FREECAD ASSEMBLY — COMPONENT RECIPES ("asm_roof")

This assembly document has 11 components, labeled P0..P10 below (a component is one placed body or linked part). 3 of them carry a construction recipe — the FreeCAD feature program that regenerates the part from scratch, quoted from this document or its linked companion documents; the rest are supplied as boundary geometry only. No exploded tour is included for this assembly.
COMPONENT P0 — geometry summary ("Hexagonal Nut M4_CBALN005"; no construction recipe available for this part):
  bounding box: 8.1 x 7.0 x 3.2 mm
  tessellated surface: 2,828 triangles
  volume: 100 mm^3 (55% of its bounding box)
  symmetry: 6-fold rotationally symmetric about the z axis
COMPONENT P1 — geometry summary ("Hexagonal Nut M4_CBALN006"; no construction recipe available for this part):
  bounding box: 8.1 x 7.0 x 3.2 mm
  tessellated surface: 2,828 triangles
  volume: 100 mm^3 (55% of its bounding box)
  symmetry: 6-fold rotationally symmetric about the z axis
COMPONENT P2 — geometry summary ("Hexagonal Nut M4_CBALN007"; no construction recipe available for this part):
  bounding box: 8.1 x 7.0 x 3.2 mm
  tessellated surface: 2,828 triangles
  volume: 100 mm^3 (55% of its bounding box)
  symmetry: 6-fold rotationally symmetric about the z axis
COMPONENT P3 — geometry summary ("Hexagonal Nut M4_CBALN4"; no construction recipe available for this part):
  bounding box: 8.1 x 7.0 x 3.2 mm
  tessellated surface: 2,828 triangles
  volume: 100 mm^3 (55% of its bounding box)
  symmetry: 6-fold rotationally symmetric about the z axis
COMPONENT P4 — geometry summary ("Hexagonal Nut M5_CBALN006"; no construction recipe available for this part):
  bounding box: 9.2 x 8.0 x 4.0 mm
  tessellated surface: 3,728 triangles
  volume: 149 mm^3 (51% of its bounding box)
COMPONENT P5 — geometry summary ("Hexagonal Nut M5_CBALN007"; no construction recipe available for this part):
  bounding box: 9.2 x 8.0 x 4.0 mm
  tessellated surface: 3,728 triangles
  volume: 149 mm^3 (51% of its bounding box)
COMPONENT P6 — geometry summary ("Hexagonal Nut M5_CBALN008"; no construction recipe available for this part):
  bounding box: 9.2 x 8.0 x 4.0 mm
  tessellated surface: 3,728 triangles
  volume: 149 mm^3 (51% of its bounding box)
COMPONENT P7 — geometry summary ("Hexagonal Nut M5_CBALN5"; no construction recipe available for this part):
  bounding box: 9.2 x 8.0 x 4.0 mm
  tessellated surface: 3,728 triangles
  volume: 149 mm^3 (51% of its bounding box)
COMPONENT P8 — recipe-attached ("linear_slide_12", a linked part whose construction recipe lives in a companion FreeCAD document of the same project; that document's serialized recipe follows).
Construction recipe (the companion document, serialized — sketch geometry with constraints, then the solid features built on it; lengths are millimeters unless a unit is written):

FCSTD DOCUMENT  (FreeCAD 1.0R39109 (Git))
Label: linear_slide
License: All rights reserved
LicenseURL: https://en.wikipedia.org/wiki/All_rights_reserved
objects: Sketcher::SketchObject×1, PartDesign::Pad×1, PartDesign::Body×1
note: 6 computed .brp shape members not serialized (recipe doc carries the construction recipe); baked Part::Feature solids carry a one-line shape summary decoded from their .brp

FEATURE [Sketcher::SketchObject] Sketch
  ArcFitTolerance = 1e-06
  AttachmentSupport = -> [XY_Plane]
  FullyConstrained = true
  MakeInternals = false
  MapMode = 5
  sketch-geometry (1):
    g0: Circle CenterX=0 CenterY=0 CenterZ=0 NormalX=0 NormalY=0 NormalZ=1 AngleXU=0 Radius=6
  constraints (2):
    c: Coincident(g0,g-1)
    c: Diameter(g0) = 12
FEATURE [PartDesign::Pad] Pad
  Direction = (0,0,1)
  Length = 100
  Length2 = 10
  Profile = -> Sketch
  ReferenceAxis = -> Sketch [N_Axis]
  Refine = true
  Suppressed = false
  Type = 0
FEATURE [PartDesign::Body] Body  label="linear_slide_12"
  AllowCompound = false
  Group = -> [Sketch,Pad]
  Origin = -> Origin
  Tip = -> Pad
COMPONENT P9 — same part as P8; its construction recipe is shown at P8.
COMPONENT P10 — recipe-attached ("plate_roof", a linked part whose construction recipe lives in a companion FreeCAD document of the same project; that document's serialized recipe follows).
Construction recipe (the companion document, serialized — sketch geometry with constraints, then the solid features built on it; lengths are millimeters unless a unit is written):

FCSTD DOCUMENT  (FreeCAD 1.0R38641 +468 (Git))
Label: plate_roof
License: All rights reserved
LicenseURL: https://en.wikipedia.org/wiki/All_rights_reserved
objects: TechDraw::DrawViewDimension×10, TechDraw::DrawProjGroupItem×2, Sketcher::SketchObject×1, PartDesign::Pad×1, PartDesign::Body×1, TechDraw::DrawSVGTemplate×1, TechDraw::DrawProjGroup×1, TechDraw::DrawPage×1
note: 22 computed .brp shape members not serialized (recipe doc carries the construction recipe); baked Part::Feature solids carry a one-line shape summary decoded from their .brp

FEATURE [Sketcher::SketchObject] Sketch
  ArcFitTolerance = 1e-06
  AttachmentSupport = -> [XY_Plane]
  FullyConstrained = false
  MakeInternals = false
  MapMode = 5
  sketch-geometry (16):
    g0: LineSegment StartX=-100 StartY=200 StartZ=0 EndX=-100 EndY=-200 EndZ=0
    g1: LineSegment StartX=-100 StartY=-200 StartZ=0 EndX=100 EndY=-200 EndZ=0
    g2: LineSegment StartX=100 StartY=-200 StartZ=0 EndX=100 EndY=200 EndZ=0
    g3: LineSegment StartX=100 StartY=200 StartZ=0 EndX=-100 EndY=200 EndZ=0
    g4: Circle CenterX=-44 CenterY=50.2 CenterZ=0 NormalX=0 NormalY=0 NormalZ=1 AngleXU=0 Radius=2.45
    g5: Circle CenterX=-44 CenterY=-157.8 CenterZ=0 NormalX=0 NormalY=0 NormalZ=1 AngleXU=0 Radius=2.45
    g6: Circle CenterX=44 CenterY=50.2 CenterZ=0 NormalX=0 NormalY=0 NormalZ=1 AngleXU=0 Radius=2.45
    g7: Circle CenterX=44 CenterY=-157.8 CenterZ=0 NormalX=0 NormalY=0 NormalZ=1 AngleXU=0 Radius=2.45
    g8: Circle [constr] CenterX=0 CenterY=0 CenterZ=0 NormalX=0 NormalY=0 NormalZ=1 AngleXU=0 Radius=9.44112
    g9: Circle CenterX=-38 CenterY=-35.8 CenterZ=0 NormalX=0 NormalY=0 NormalZ=1 AngleXU=0 Radius=1.95
    g10: Circle CenterX=-38 CenterY=-71.8 CenterZ=0 NormalX=0 NormalY=0 NormalZ=1 AngleXU=0 Radius=1.95
    g11: Circle CenterX=-38 CenterY=-53.8 CenterZ=0 NormalX=0 NormalY=0 NormalZ=1 AngleXU=0 Radius=6.5
    g12: Circle CenterX=38 CenterY=-35.8 CenterZ=0 NormalX=0 NormalY=0 NormalZ=1 AngleXU=0 Radius=1.95
    g13: Circle CenterX=38 CenterY=-53.8 CenterZ=0 NormalX=0 NormalY=0 NormalZ=1 AngleXU=0 Radius=6.5
    g14: Circle CenterX=38 CenterY=-71.8 CenterZ=0 NormalX=0 NormalY=0 NormalZ=1 AngleXU=0 Radius=1.95
    g15: LineSegment [constr] StartX=0 StartY=0 StartZ=0 EndX=0 EndY=174.663 EndZ=0
  constraints (44):
    c: Coincident(g0,g1)
    c: Coincident(g1,g2)
    c: Coincident(g2,g3)
    c: Coincident(g3,g0)
    c: Vertical(g0)
    c: Vertical(g2)
    c: Horizontal(g1)
    c: Horizontal(g3)
    c: DistanceY(g0,g0) = 400
    c: DistanceX(g3,g3) = 200
    c: Vertical(g4,g5)
    c: Diameter(g4) = 4.9
    c: Equal(g4,g5)
    c: DistanceY(g5,g4) = 208
    c: Horizontal(g6,g4)
    c: Horizontal(g7,g5)
    c: Equal(g6,g4)
    c: Equal(g4,g7)
    c: DistanceX(g4,g6) = 88
    c: Vertical(g7,g6)
    c: DistanceY(g8,g4) = 50.2
    c: DistanceX(g4,g8) = 44
    c: Distance(g8,g3) = 200
    c: Distance(g8,g0) = 100
    c: Vertical(g9,g11)
    c: Vertical(g11,g10)
    c: Vertical(g12,g13)
    c: Vertical(g13,g14)
    c: DistanceY(g11,g9) = 18
    c: DistanceY(g10,g11) = 18
    c: Diameter(g9) = 3.9
    c: Equal(g9,g10)
    c: Equal(g10,g12)
    c: Equal(g12,g14)
    c: Horizontal(g9,g12)
    c: Horizontal(g10,g14)
    c: Equal(g11,g13)
    c: Diameter(g11) = 13
    c: DistanceX(g11,g8) = 38
    c: Horizontal(g11,g13)
    c: DistanceY(g11,g4) = 104
    c: Coincident(g15,g8)
    c: Symmetric(g11,g13,g15)
    c: Coincident(g8,g-1)
FEATURE [PartDesign::Pad] Pad
  Direction = (0,0,1)
  Length = 3
  Length2 = 10
  Profile = -> Sketch
  ReferenceAxis = -> Sketch [N_Axis]
  Refine = true
  Suppressed = false
  Type = 0
FEATURE [PartDesign::Body] Body  label="plate_roof"
  AllowCompound = false
  Group = -> [Sketch,Pad]
  Origin = -> Origin
  Tip = -> Pad
FEATURE [TechDraw::DrawSVGTemplate] Template
  EditableTexts = approval_person=B. Hecate; creator=Djordje Vujic; date_of_issue=20.1.25.; document_type=Assembly Drawing; general_tolerances=ISO 2768-m; identification_number=DN; language_code=EN; part_material=Stainless steel Mat.No. 1.4301; revision_index=AAA; sheet_number=1 / 3; sheet_scale=1 : 2; title=plate_roof
  Height = 297
  Orientation = 0
  Template = /snap/freecad/1248/usr/share/Mod/TechDraw/Templates/A4_Portrait_ISO5457_minimal.svg
  Width = 210
FEATURE [TechDraw::DrawProjGroupItem] ProjItem  label="Front"
  CoarseView = false
  Direction = (0,0,1)
  Focus = 100
  HardHidden = false
  IsoCount = 0
  IsoHidden = false
  IsoVisible = false
  LockPosition = true
  Perspective = false
  Rotation = 0
  RotationVector = (1,0,0)
  Scale = 0.5
  ScaleType = 0
  ScrubCount = 1
  SeamHidden = false
  SeamVisible = false
  SmoothHidden = false
  SmoothVisible = true
  Source = -> [Body]
  Type = 0
  X = 0
  XDirection = (1,0,0)
  Y = 0
FEATURE [TechDraw::DrawProjGroupItem] ProjItem001  label="Bottom"
  CoarseView = false
  Direction = (0,-1,0)
  Focus = 100
  HardHidden = false
  IsoCount = 0
  IsoHidden = false
  IsoVisible = false
  LockPosition = false
  Perspective = false
  Rotation = 0
  RotationVector = (1,0,0)
  Scale = 0.5
  ScaleType = 0
  ScrubCount = 1
  SeamHidden = false
  SeamVisible = false
  SmoothHidden = false
  SmoothVisible = true
  Source = -> [Body]
  Type = 5
  X = 0
  XDirection = (1,0,0)
  Y = 115.75
FEATURE [TechDraw::DrawProjGroup] ProjGroup
  Anchor = -> ProjItem
  AutoDistribute = true
  LockPosition = false
  ProjectionType = 0
  Rotation = 0
  Scale = 0.5
  ScaleType = 2
  Source = -> [Body]
  Views = -> [ProjItem,ProjItem001]
  X = 105
  Y = 162.983
  spacingX = 15
  spacingY = 15
FEATURE [TechDraw::DrawViewDimension] Dimension
  AngleOverride = false
  Arbitrary = false
  ArbitraryTolerances = false
  BoxCorners = (2) [(-50,-0.75,0),(50,0.75,0)]
  EqualTolerance = true
  ExtensionAngle = 0
  FormatSpec = %.2w
  FormatSpecOverTolerance = %+.2w
  FormatSpecUnderTolerance = %+.2w
  Inverted = false
  LineAngle = 0
  LockPosition = false
  MeasureType = 1
  OverTolerance = 0
  References2D = -> [ProjItem001]
  Rotation = 0
  ScaleType = 0
  TheoreticalExact = false
  Type = 2
  UnderTolerance = 0
  X = -62.2509
  Y = -6.95305
FEATURE [TechDraw::DrawViewDimension] Dimension001
  AngleOverride = false
  Arbitrary = false
  ArbitraryTolerances = false
  BoxCorners = (2) [(-50,-0.75,0),(50,0.75,0)]
  EqualTolerance = true
  ExtensionAngle = 0
  FormatSpec = %.2w
  FormatSpecOverTolerance = %+.2w
  FormatSpecUnderTolerance = %+.2w
  Inverted = false
  LineAngle = 0
  LockPosition = false
  MeasureType = 1
  OverTolerance = 0
  References2D = -> [ProjItem001]
  Rotation = 0
  ScaleType = 0
  TheoreticalExact = false
  Type = 1
  UnderTolerance = 0
  X = 0
  Y = -5.41651
FEATURE [TechDraw::DrawViewDimension] Dimension002
  AngleOverride = false
  Arbitrary = false
  ArbitraryTolerances = false
  BoxCorners = (2) [(-50,-100,0),(50,100,0)]
  EqualTolerance = true
  ExtensionAngle = 0
  FormatSpec = %.2w
  FormatSpecOverTolerance = %+.2w
  FormatSpecUnderTolerance = %+.2w
  Inverted = false
  LineAngle = 0
  LockPosition = false
  MeasureType = 1
  OverTolerance = 0
  References2D = -> [ProjItem]
  Rotation = 0
  ScaleType = 0
  TheoreticalExact = false
  Type = 2
  UnderTolerance = 0
  X = -64.6458
  Y = 3.29053
FEATURE [TechDraw::DrawViewDimension] Dimension003
  AngleOverride = false
  Arbitrary = false
  ArbitraryTolerances = false
  BoxCorners = (2) [(-50,-100,0),(50,100,0)]
  EqualTolerance = true
  ExtensionAngle = 0
  FormatSpec = %.2w
  FormatSpecOverTolerance = %+.2w
  FormatSpecUnderTolerance = %+.2w
  Inverted = false
  LineAngle = 0
  LockPosition = false
  MeasureType = 1
  OverTolerance = 0
  References2D = -> [ProjItem]
  Rotation = 0
  ScaleType = 0
  TheoreticalExact = false
  Type = 0
  UnderTolerance = 0
  X = 29.0917
  Y = -31.4
FEATURE [TechDraw::DrawViewDimension] Dimension004
  AngleOverride = false
  Arbitrary = false
  ArbitraryTolerances = false
  BoxCorners = (2) [(-50,-100,0),(50,100,0)]
  EqualTolerance = true
  ExtensionAngle = 0
  FormatSpec = %.2w
  FormatSpecOverTolerance = %+.2w
  FormatSpecUnderTolerance = %+.2w
  Inverted = false
  LineAngle = 0
  LockPosition = false
  MeasureType = 1
  OverTolerance = 0
  References2D = -> [ProjItem]
  Rotation = 0
  ScaleType = 0
  TheoreticalExact = false
  Type = 0
  UnderTolerance = 0
  X = 0
  Y = -5.52183
FEATURE [TechDraw::DrawViewDimension] Dimension005
  AngleOverride = false
  Arbitrary = false
  ArbitraryTolerances = false
  BoxCorners = (2) [(-50,-100,0),(50,100,0)]
  EqualTolerance = true
  ExtensionAngle = 0
  FormatSpec = %.2w
  FormatSpecOverTolerance = %+.2w
  FormatSpecUnderTolerance = %+.2w
  Inverted = false
  LineAngle = 0
  LockPosition = false
  MeasureType = 1
  OverTolerance = 0
  References2D = -> [ProjItem]
  Rotation = 0
  ScaleType = 0
  TheoreticalExact = false
  Type = 0
  UnderTolerance = 0
  X = -34.5
  Y = -5.52183
FEATURE [TechDraw::DrawViewDimension] Dimension006
  AngleOverride = false
  Arbitrary = false
  ArbitraryTolerances = false
  BoxCorners = (2) [(-50,-100,0),(50,100,0)]
  EqualTolerance = true
  ExtensionAngle = 0
  FormatSpec = %.2w
  FormatSpecOverTolerance = %+.2w
  FormatSpecUnderTolerance = %+.2w
  Inverted = false
  LineAngle = 0
  LockPosition = false
  MeasureType = 1
  OverTolerance = 0
  References2D = -> [ProjItem]
  Rotation = 0
  ScaleType = 0
  TheoreticalExact = false
  Type = 0
  UnderTolerance = 0
  X = -33.0527
  Y = -22.4
FEATURE [TechDraw::DrawViewDimension] Dimension007
  AngleOverride = false
  Arbitrary = false
  ArbitraryTolerances = false
  BoxCorners = (2) [(-50,-100,0),(50,100,0)]
  EqualTolerance = false
  ExtensionAngle = 0
  FormatSpec = ⌀%.2w
  FormatSpecOverTolerance = %+.2w
  FormatSpecUnderTolerance = -%.2w
  Inverted = false
  LineAngle = 0
  LockPosition = false
  MeasureType = 1
  OverTolerance = 1
  References2D = -> [ProjItem]
  Rotation = 0
  ScaleType = 0
  TheoreticalExact = false
  Type = 5
  UnderTolerance = 0.9
  X = -9.88409
  Y = -19.3744
FEATURE [TechDraw::DrawViewDimension] Dimension008
  AngleOverride = false
  Arbitrary = false
  ArbitraryTolerances = false
  BoxCorners = (2) [(-50,-100,0),(50,100,0)]
  EqualTolerance = true
  ExtensionAngle = 0
  FormatSpec = %.2w
  FormatSpecOverTolerance = %+.2w
  FormatSpecUnderTolerance = %+.2w
  Inverted = false
  LineAngle = 0
  LockPosition = false
  MeasureType = 1
  OverTolerance = 1
  References2D = -> [ProjItem]
  Rotation = 0
  ScaleType = 0
  TheoreticalExact = false
  Type = 0
  UnderTolerance = -1
  X = 9.62605
  Y = -67.95
FEATURE [TechDraw::DrawViewDimension] Dimension009
  AngleOverride = false
  Arbitrary = false
  ArbitraryTolerances = false
  BoxCorners = (2) [(-50,-100,0),(50,100,0)]
  EqualTolerance = false
  ExtensionAngle = 0
  FormatSpec = ⌀%.2w
  FormatSpecOverTolerance = %+.2w
  FormatSpecUnderTolerance = -%.2w
  Inverted = false
  LineAngle = 0
  LockPosition = false
  MeasureType = 1
  OverTolerance = 0.1
  References2D = -> [ProjItem]
  Rotation = 0
  ScaleType = 0
  TheoreticalExact = false
  Type = 5
  UnderTolerance = 0
  X = -5.75191
  Y = -38.5146
FEATURE [TechDraw::DrawPage] Page
  KeepUpdated = true
  NextBalloonIndex = 1
  ProjectionType = 0
  Template = -> Template
  Views = -> [ProjGroup,Dimension,Dimension001,Dimension002,Dimension003,Dimension004,Dimension005,Dimension006,Dimension007,Dimension008,Dimension009]
PROVENANCE & LICENSES
A FreeCAD (.FCStd) document from a public repository crawl; recipes are the document's own serialized feature recipes (and, for linked parts, companion documents' recipes).
License: as declared in the source repository (recorded in the dataset sidecar).
